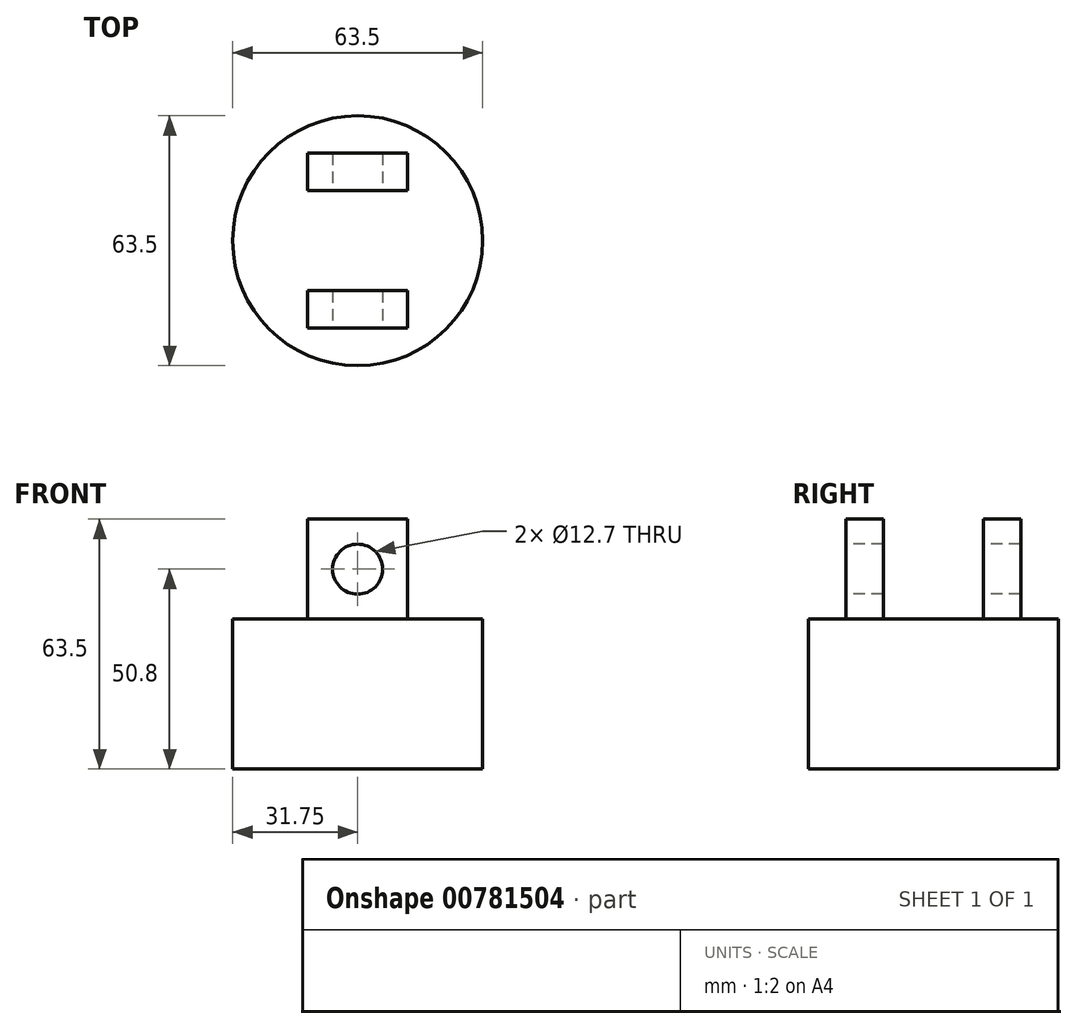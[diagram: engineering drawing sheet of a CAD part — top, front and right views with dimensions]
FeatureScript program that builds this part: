
annotation { "Feature Type Name" : "Feature", "Feature Type Description" : "" }
export const myFeature = defineFeature(function(context is Context, id is Id, definition is map)
    precondition{}
    {
        {
            var Q0;
            Q0=qCreatedBy(makeId("Top.planeOp"),FACE);
            var sketch = newSketch(context, id + "F0", { "sketchPlane" : qUnion([Q0])});
            skCircle(sketch, "E0", {"center": v(0, 0) * mm, "radius": 31.75 * mm});
            skSolve(sketch);
        }
        {
            var Q0;
            Q0=makeQuery(id+"F0.imprint","IMPRINT",FACE,{"disambiguationData":[TD([[makeQuery(id+"F0.imprint","IMPRINT",EDGE,{"derivedFrom":sQuery(id+"F0.wireOp",EDGE,"E0")}),1.0]])]});
            extrude(context, id + "F1", {"entities" : qUnion([Q0]), "depth" : 38.1 * mm, "offsetDistance" : 25.4 * mm});
        }
        {
            var Q0;
            Q0=makeQuery(id+"F1.opExtrude","CAP_FACE",FACE,{"disambiguationData":[OSD([sQuery(id+"F0.wireOp",EDGE,"E0")])],"isStart":false});
            var sketch = newSketch(context, id + "F2", { "sketchPlane" : qUnion([Q0])});
            skLineSegment(sketch, "E1.bottom", {"start": v(12.7, 22.23) * mm, "end": v(-12.7, 22.23) * mm});
            skLineSegment(sketch, "E1.top", {"start": v(12.7, 12.7) * mm, "end": v(-12.7, 12.7) * mm});
            skLineSegment(sketch, "E1.left", {"start": v(-12.7, 22.23) * mm, "end": v(-12.7, 12.7) * mm});
            skLineSegment(sketch, "E1.right", {"start": v(12.7, 22.23) * mm, "end": v(12.7, 12.7) * mm});
            skPoint(sketch, "E1.middle", {"position": v(0, 17.46) * mm});
            skLineSegment(sketch, "E2.bottom", {"start": v(12.7, -12.7) * mm, "end": v(-12.7, -12.7) * mm});
            skLineSegment(sketch, "E2.top", {"start": v(12.7, -22.23) * mm, "end": v(-12.7, -22.23) * mm});
            skLineSegment(sketch, "E2.left", {"start": v(-12.7, -12.7) * mm, "end": v(-12.7, -22.23) * mm});
            skLineSegment(sketch, "E2.right", {"start": v(12.7, -12.7) * mm, "end": v(12.7, -22.23) * mm});
            skPoint(sketch, "E2.middle", {"position": v(0, -17.46) * mm});
            skLineSegment(sketch, "E3", {"start": v(0, 12.7) * mm, "end": v(0, -12.7) * mm, "construction": true});
            skSolve(sketch);
        }
        {
            var Q0;
            Q0 = qSketchRegion(id + "F2", true);
            extrude(context, id + "F3", {"entities" : qUnion([Q0]), "operationType" : NewBodyOperationType.ADD, "depth" : 25.4 * mm, "offsetDistance" : 25.4 * mm});
        }
        {
            var Q0;
            Q0=makeQuery(id+"F3.opExtrude","SWEPT_FACE",FACE,{"disambiguationData":[OSD([sQuery(id+"F2.wireOp",EDGE,"E2.top")])]});
            var sketch = newSketch(context, id + "F4", { "sketchPlane" : qUnion([Q0])});
            skCircle(sketch, "E4", {"center": v(0, 50.8) * mm, "radius": 6.35 * mm});
            skPoint(sketch, "E4.centerSnap0", {"position": v(-12.7, 50.8) * mm});
            skSolve(sketch);
        }
        {
            var Q0;
            Q0=makeQuery(id+"F4.imprint","IMPRINT",FACE,{"disambiguationData":[TD([[makeQuery(id+"F4.imprint","IMPRINT",EDGE,{"derivedFrom":sQuery(id+"F4.wireOp",EDGE,"E4")}),1.0]])]});
            var Q1;
            Q1=makeQuery(id+"F3.opExtrude","SWEPT_FACE",FACE,{"disambiguationData":[OSD([sQuery(id+"F2.wireOp",EDGE,"E1.bottom")])]});
            extrude(context, id + "F5", {"entities" : qUnion([Q0]), "operationType" : NewBodyOperationType.REMOVE, "endBound" : BoundingType.UP_TO_SURFACE, "oppositeDirection" : true, "depth" : 25.4 * mm, "endBoundEntityFace" : qUnion([Q1]), "offsetDistance" : 25.4 * mm});
        }
    });
